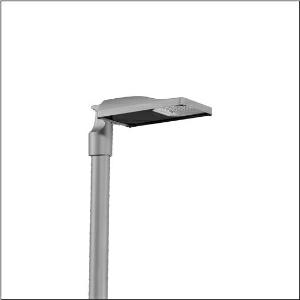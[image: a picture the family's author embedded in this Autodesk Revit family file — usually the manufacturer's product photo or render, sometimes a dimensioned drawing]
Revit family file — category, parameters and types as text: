
# Revit family: streetlight_sl_31_micro___st1_0a_5xh1d71b08ca_ebbd
name_source: partatom
category: Lighting Fixtures
units: mm (PartAtom-declared; Revit-internal decimal feet)

## family parameters
Cut with Voids When Loaded = No
Host = Face
Light Source = No
Part Type = Normal
Room Calculation Point = No
Round Connector Dimension = Use Diameter
Shared = No

## types (1)
- --- (1 x LED, 1170 lm, 10.3 W, 2200K)
    Apparent Load = 10 VA
    CIE Flux Codes = 37 72 97 100 100
    Color Rendering = 70
    Color Temperature = 2200K
    Default Elevation = 1800 mm
    Description = Streetlight SL 31 micro Easy, LST, Desk-Remote mast luminaire for post-top, side-entry; light control with lens of PMMA; light distribution: ST1.0a, direct asymmetric distribution, for standard-compliant lighting for roads and squares; LED: luminous flux: 1.170lm, light colour: 722, colour temperature: 2200K; luminous efficacy: 113,6lm/W; control: pre-setting: linear dimming characteristic, flexible luminous flux parameterisation, time-dependent luminous flux control, constant luminous flux control, power reduction, intelligent temperature release in ECG and LED module, overheat protection; luminaire housing, of diecast aluminium, SITECO metallic grey (DB 702S), corrosivity category C5 high according to DIN EN ISO 12944; cover of toughened safety glass, transparent, mast flange of diecast aluminium, SITECO metallic grey (DB 702S), spigot size: 76/60mm, mast flange included unmounted; cable length: 5,5m, connection cable pre-assembled; mains connection: 220..240V, AC, 50/60Hz; power consumption (at start of service life): 10,3W / (at end of service life): 10,6W / (with reduced operation 50%): 5,3W; protection rating (complete): IP66; insulation class (complete): insulation class II (safety insulation); impact resistance: IK10; certification: CE, ENEC, ENEC+, VDE, UKCA; permissible operating ambient temperature for outdoor applications: -40..+50°C; packaging unit: 1 piece

Light Distribution: ST1.0a
    Height = 76 mm
    Lamp = 1 x LED
    Lamp Light Flux = 1170 lm
    Lamp Power = 10.3 W
    Lamp count = 1
    Length = 467 mm
    Luminous efficacy = 114 lm/W
    Manufacturer = Siteco
    ModVariant = No
    Model = 5XH1D71B08CA
    Mounting Place = Pole
    Mounting Type = Pole top
    Number of Poles = 1
    OnlyDefault = Yes
    Power Factor = 1
    Product Name = Streetlight SL 31 micro | ST1.0a
    Product group = mast luminaire | pylon top
    ProductGroupID = 6100
    Protection Class = Protection class II
    Protection Degree = IP 66
    RLX_Detail_Level = 1
    RLX_Emergency_Light_Flux = 0 lm
    RLX_Emergency_Type = 0
    RLX_Emergency_Type_DB = No
    RlxData = <blob elided: 22497 chars, md5=dcde6482>
    Socket = socket
    Standby Power = 0 W
    System Light Flux = 1170 lm
    System Power = 10 W
    Type Comments = factory setting: luminous flux: 100 % | dim-lin: 254 | 386 mA
    Type Image = l_1300309.jpg
    URL = http://relux.com
    VarID = @adj_011193
    Voltage = 0 V
    Weight = 0.00 kg
    Width = 265 mm

## geometry (parser evidence)
native form markers: Blend x4, Sweep x10
no freeform markers — native parametric forms only
